# Revit family: Gymnasium-Eqpt_Basketball_IPIbyBison_IP12WF
name_source: partatom
category: Specialty Equipment
revit_build: Autodesk Revit 2018 (Build: 20170927_1515(x64)
units: mm (PartAtom-declared; Revit-internal decimal feet)

## family parameters
Always vertical = No
Cut with Voids When Loaded = No
Part Type = Normal
Room Calculation Point = No
Round Connector Dimension = Use Diameter
Shared = No
Work Plane-Based = Yes

## types (1)
- Wall Mounted Fold Up
    Default Elevation = 0' - 0"
    Description = IPI by Bison Wall Mounted Up Folding Basketball Backboard - IP12WF as Specified
    Expected Lifespan (Years) = 0
    Maintenance Schedule (Months) = 0
    Manufacturer = IPI by Bison
    Manufacturer Fax = 800-638-0698
    Manufacturer Website = https://ipibybison.com
    Model = IP12WF
    Product Data = http://www.arcat.com
    Revision = R1_01-2018
    Sales Information = https://ipibybison.com
    URL = https://ipibybison.com
    Unit Depth = 2' - 8"
    Unit Width = 7' - 0"
    Warranty Duration (Years) = 0
    wall distance text = 4 to 10 ft from Wall

## geometry (parser evidence)
native form markers: Sweep x4
no freeform markers — native parametric forms only
